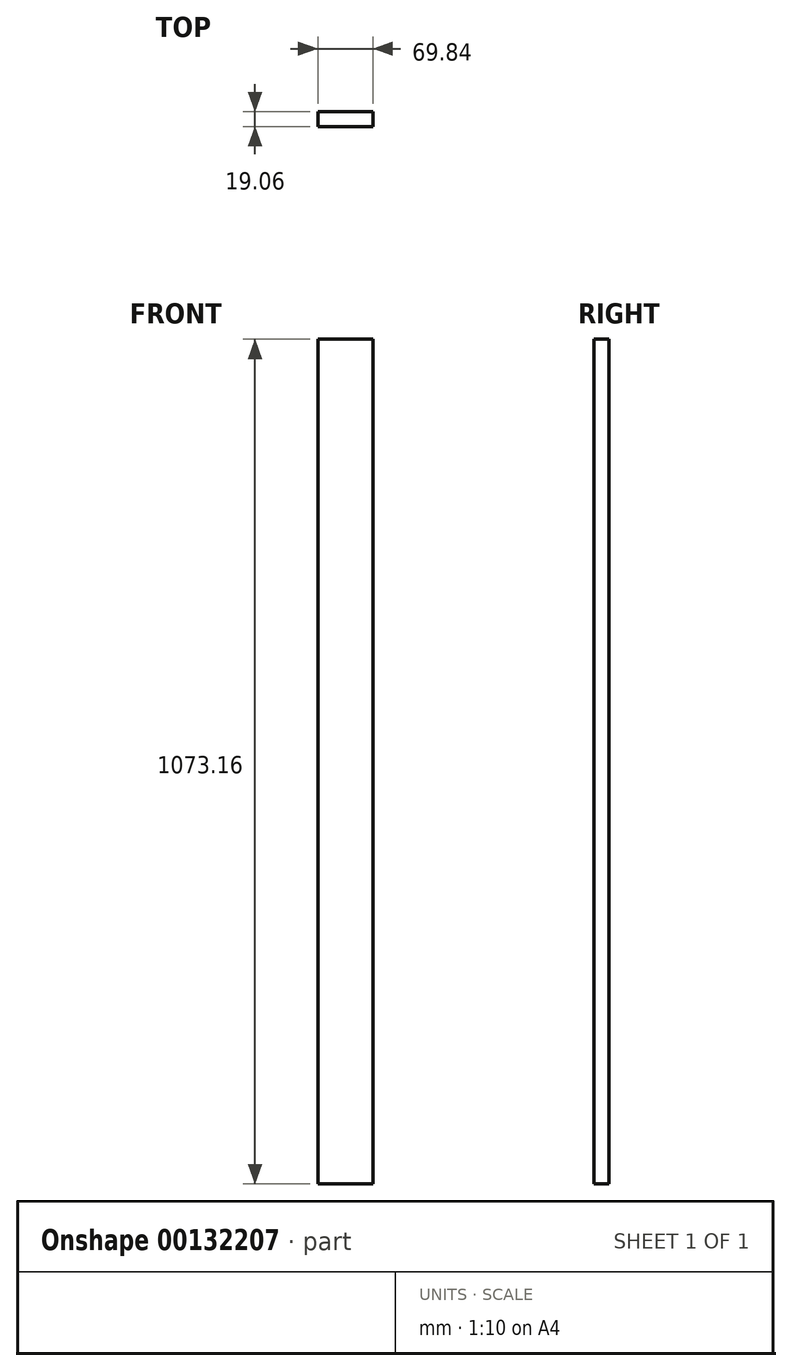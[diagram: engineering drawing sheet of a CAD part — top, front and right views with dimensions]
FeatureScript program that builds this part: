
annotation { "Feature Type Name" : "Feature", "Feature Type Description" : "" }
export const myFeature = defineFeature(function(context is Context, id is Id, definition is map)
    precondition{}
    {
        {
            var Q0;
            Q0=qCreatedBy(makeId("Front.planeOp"),FACE);
            var sketch = newSketch(context, id + "F0", { "sketchPlane" : qUnion([Q0])});
            skLineSegment(sketch, "E0.bottom", {"start": v(-34.92, -536.58) * mm, "end": v(34.93, -536.58) * mm});
            skLineSegment(sketch, "E0.top", {"start": v(-34.93, 536.58) * mm, "end": v(34.92, 536.58) * mm});
            skLineSegment(sketch, "E0.left", {"start": v(-34.92, -536.58) * mm, "end": v(-34.93, 536.58) * mm});
            skLineSegment(sketch, "E0.right", {"start": v(34.93, -536.58) * mm, "end": v(34.92, 536.58) * mm});
            skPoint(sketch, "E0.middle", {"position": v(0, 0) * mm});
            skSolve(sketch);
        }
        {
            var Q0;
            Q0=makeQuery(id+"F0.imprint","IMPRINT",FACE,{"disambiguationData":[TD([[makeQuery(id+"F0.imprint","IMPRINT",EDGE,{"derivedFrom":sQuery(id+"F0.wireOp",EDGE,"E0.bottom")}),1.0]])]});
            extrude(context, id + "F1", {"entities" : qUnion([Q0]), "endBound" : BoundingType.SYMMETRIC, "depth" : 19.05 * mm});
        }
    });
